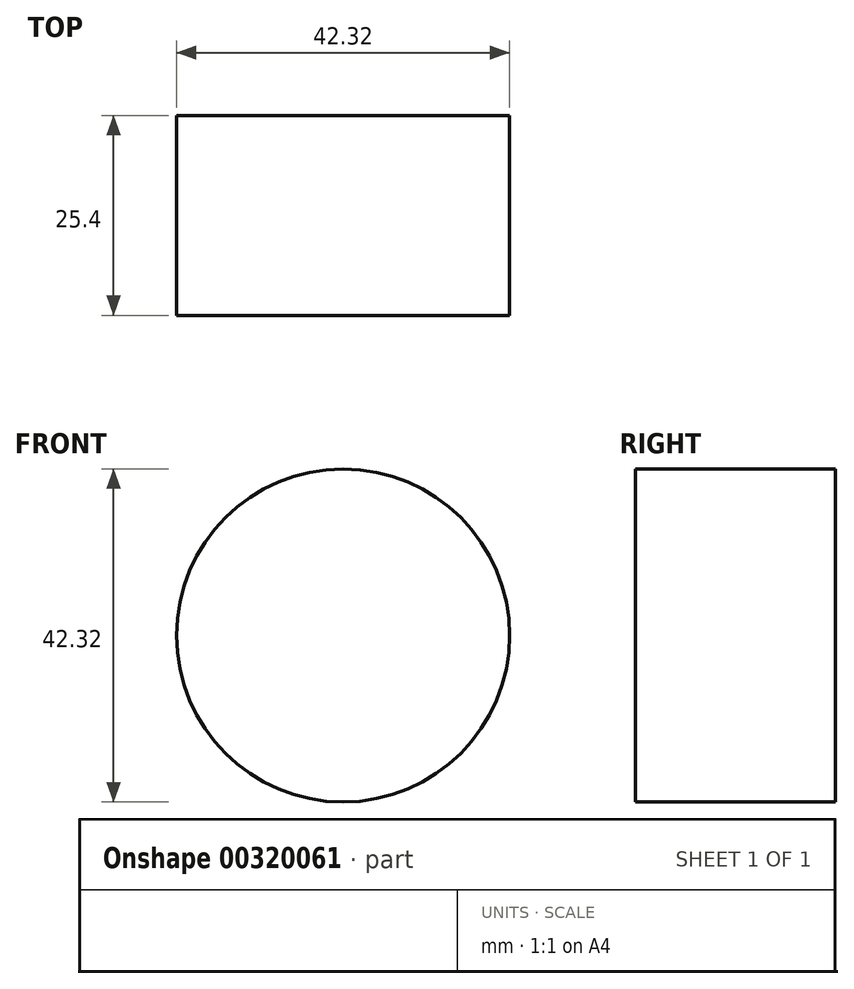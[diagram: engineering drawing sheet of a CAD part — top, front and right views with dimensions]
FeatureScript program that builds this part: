
annotation { "Feature Type Name" : "Feature", "Feature Type Description" : "" }
export const myFeature = defineFeature(function(context is Context, id is Id, definition is map)
    precondition{}
    {
        {
            var Q0;
            Q0=qCreatedBy(makeId("Front.planeOp"),FACE);
            var sketch = newSketch(context, id + "F0", { "sketchPlane" : qUnion([Q0])});
            skCircle(sketch, "E0", {"center": v(0, 0) * mm, "radius": 21.16 * mm});
            skSolve(sketch);
        }
        {
            var Q0;
            Q0=makeQuery(id+"F0.imprint","IMPRINT",FACE,{"disambiguationData":[TD([[makeQuery(id+"F0.imprint","IMPRINT",EDGE,{"derivedFrom":sQuery(id+"F0.wireOp",EDGE,"E0")}),1.0]])]});
            extrude(context, id + "F1", {"entities" : qUnion([Q0]), "depth" : 25.4 * mm});
        }
    });
